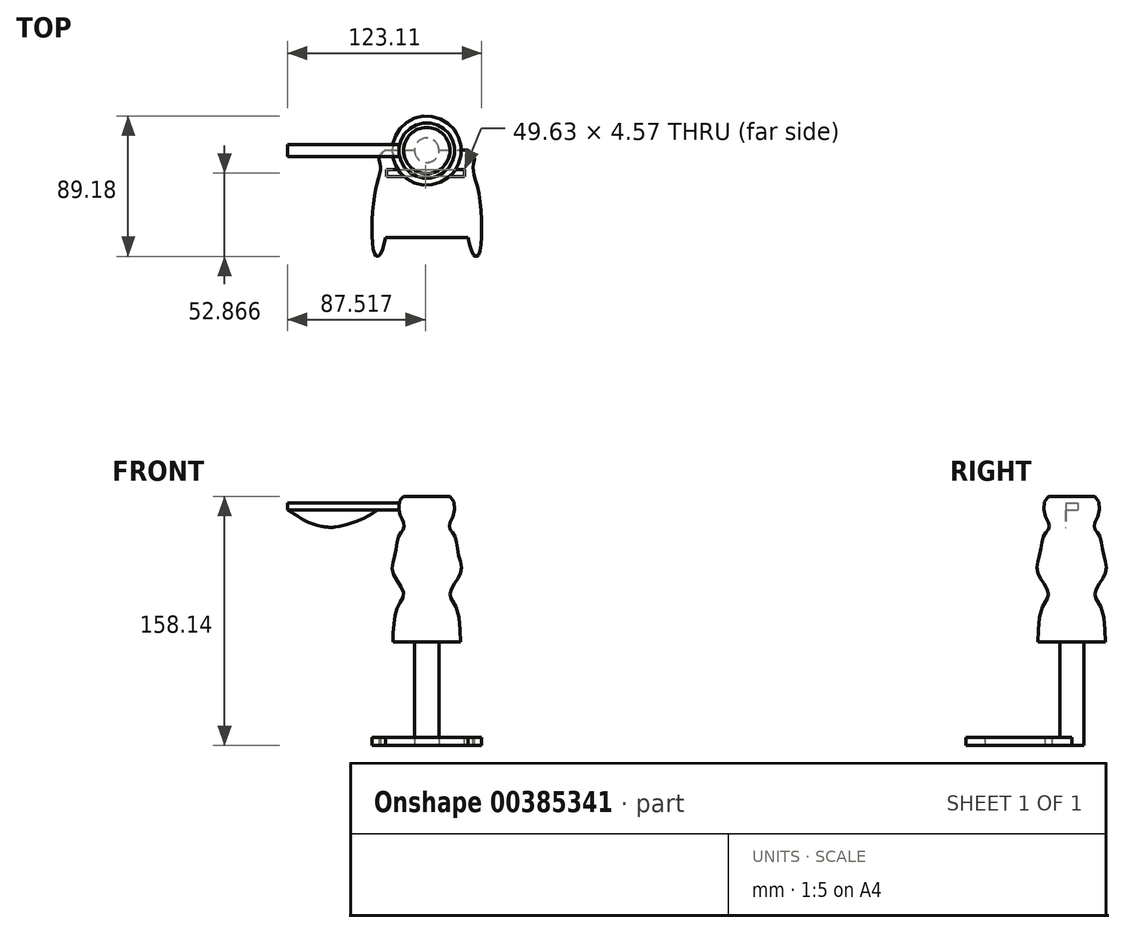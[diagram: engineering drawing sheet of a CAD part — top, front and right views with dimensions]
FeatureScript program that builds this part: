
annotation { "Feature Type Name" : "Feature", "Feature Type Description" : "" }
export const myFeature = defineFeature(function(context is Context, id is Id, definition is map)
    precondition{}
    {
        {
            var Q0;
            Q0=qCreatedBy(makeId("Top.planeOp"),FACE);
            var sketch = newSketch(context, id + "F0", { "sketchPlane" : qUnion([Q0])});
            skLineSegment(sketch, "E0", {"start": v(0, 55.4) * mm, "end": v(-26.25, 55.4) * mm});
            skFitSpline(sketch, "E1", {"points": [v(-26.25, 55.4) * mm, v(-30.26, 51.03) * mm, v(-29.53, 45.57) * mm, v(-29.9, 40.46) * mm, v(-33.17, 26.97) * mm, v(-34.63, 0) * mm, v(-32.44, -11.66) * mm, v(-30.26, -11.66) * mm, v(-26.25, 0) * mm], "startDerivative": vector(-53.73, -39.81) * mm, "endDerivative": vector(23.9, 106.11) * mm});
            skLineSegment(sketch, "E2", {"start": v(-26.25, 0) * mm, "end": v(0, 0) * mm});
            skLineSegment(sketch, "E3.MirrorCS", {"start": v(0, 55.4) * mm, "end": v(26.25, 55.4) * mm});
            skFitSpline(sketch, "E4.MirrorCS", {"points": [v(26.25, 55.4) * mm, v(30.26, 51.03) * mm, v(29.53, 45.57) * mm, v(29.9, 40.46) * mm, v(33.17, 26.97) * mm, v(34.63, 0) * mm, v(32.44, -11.66) * mm, v(30.26, -11.66) * mm, v(26.25, 0) * mm], "startDerivative": vector(53.73, -39.81) * mm, "endDerivative": vector(-23.9, 106.11) * mm});
            skLineSegment(sketch, "E5.MirrorCS", {"start": v(26.25, 0) * mm, "end": v(0, 0) * mm});
            skSolve(sketch);
        }
        {
            var Q0;
            Q0 = qSketchRegion(id + "F0", true);
            extrude(context, id + "F1", {"entities" : qUnion([Q0]), "depth" : 5.08 * mm});
        }
        {
            var Q0;
            Q0=qCreatedBy(makeId("Top.planeOp"),FACE);
            var sketch = newSketch(context, id + "F2", { "sketchPlane" : qUnion([Q0])});
            skCircle(sketch, "E6", {"center": v(0, 55.28) * mm, "radius": 7.77 * mm});
            skSolve(sketch);
        }
        {
            var Q0;
            Q0 = qSketchRegion(id + "F2", true);
            extrude(context, id + "F3", {"entities" : qUnion([Q0]), "operationType" : NewBodyOperationType.ADD, "depth" : 66.04 * mm});
        }
        {
            var Q0;
            Q0=qCreatedBy(makeId("Front.planeOp"),FACE);
            cPlane(context, id + "F4", {"entities" : qUnion([Q0]), "cplaneType" : CPlaneType.OFFSET, "offset" : 55.12 * mm, "oppositeDirection" : true, "width" : 152.4 * mm, "height" : 152.4 * mm});
        }
        {
            var Q0;
            Q0=qCreatedBy(id+"F4.planeOp",FACE);
            var sketch = newSketch(context, id + "F5", { "sketchPlane" : qUnion([Q0])});
            skLineSegment(sketch, "E7", {"start": v(0, 53.83) * mm, "end": v(0, 158.14) * mm, "construction": true});
            skLineSegment(sketch, "E8", {"start": v(0, 158.14) * mm, "end": v(-14.7, 158.14) * mm});
            skFitSpline(sketch, "E9", {"points": [v(-14.7, 158.14) * mm, v(-17.03, 155.35) * mm, v(-17.03, 146.52) * mm, v(-14.7, 141.88) * mm, v(-14.7, 137.46) * mm, v(-17.5, 133.75) * mm, v(-20.28, 120.97) * mm, v(-21.44, 109.36) * mm, v(-14.7, 96.81) * mm, v(-18.65, 87.52) * mm, v(-21.44, 65.68) * mm], "startDerivative": vector(-42.25, -32.32) * mm, "endDerivative": vector(-3.32, -157.38) * mm});
            skLineSegment(sketch, "E10", {"start": v(-21.44, 65.68) * mm, "end": v(0, 65.68) * mm});
            skLineSegment(sketch, "E11", {"start": v(0, 65.68) * mm, "end": v(0, 158.14) * mm});
            skSolve(sketch);
        }
        {
            var Q0;
            Q0 = qSketchRegion(id + "F5", true);
            var Q1;
            Q1=sQuery(id+"F5.wireOp",EDGE,"E7");
            revolve(context, id + "F6", {"operationType" : NewBodyOperationType.ADD, "entities" : qUnion([Q0]), "axis" : qUnion([Q1]), "revolveType" : RevolveType.FULL});
        }
        {
            var Q0;
            Q0=makeQuery(id+"F1.opExtrude","CAP_FACE",FACE,{"disambiguationData":[OSD([sQuery(id+"F0.wireOp",EDGE,"E0"),sQuery(id+"F0.wireOp",EDGE,"E1"),sQuery(id+"F0.wireOp",EDGE,"E2"),sQuery(id+"F0.wireOp",EDGE,"E3.MirrorCS"),sQuery(id+"F0.wireOp",EDGE,"E4.MirrorCS"),sQuery(id+"F0.wireOp",EDGE,"E5.MirrorCS")])],"isStart":false});
            var sketch = newSketch(context, id + "F7", { "sketchPlane" : qUnion([Q0])});
            skLineSegment(sketch, "E12", {"start": v(23.95, 43.02) * mm, "end": v(23.95, 38.45) * mm});
            skLineSegment(sketch, "E13", {"start": v(23.95, 38.45) * mm, "end": v(-25.68, 38.45) * mm});
            skLineSegment(sketch, "E14", {"start": v(-25.68, 38.45) * mm, "end": v(-25.5, 43.02) * mm});
            skLineSegment(sketch, "E15", {"start": v(-25.5, 43.02) * mm, "end": v(23.95, 43.02) * mm});
            skSolve(sketch);
        }
        {
            var Q0;
            Q0=makeQuery(id+"F7.imprint","IMPRINT",FACE,{"disambiguationData":[TD([[makeQuery(id+"F7.imprint","IMPRINT",EDGE,{"derivedFrom":sQuery(id+"F7.wireOp",EDGE,"E12")}),-1.0]])]});
            extrude(context, id + "F8", {"entities" : qUnion([Q0]), "operationType" : NewBodyOperationType.REMOVE, "oppositeDirection" : true, "depth" : 25.4 * mm});
        }
        {
            var Q0;
            Q0=qCreatedBy(id+"F4.planeOp",FACE);
            var sketch = newSketch(context, id + "F9", { "sketchPlane" : qUnion([Q0])});
            skLineSegment(sketch, "E16", {"start": v(-17.51, 154.17) * mm, "end": v(-17.51, 149.68) * mm});
            skLineSegment(sketch, "E17", {"start": v(-17.51, 149.68) * mm, "end": v(-88.38, 149.68) * mm});
            skLineSegment(sketch, "E18", {"start": v(-88.38, 149.68) * mm, "end": v(-88.38, 154.17) * mm});
            skLineSegment(sketch, "E19", {"start": v(-88.38, 154.17) * mm, "end": v(-17.51, 154.17) * mm});
            skSolve(sketch);
        }
        {
            var Q0;
            Q0=makeQuery(id+"F9.imprint","IMPRINT",FACE,{"disambiguationData":[TD([[makeQuery(id+"F9.imprint","IMPRINT",EDGE,{"derivedFrom":sQuery(id+"F9.wireOp",EDGE,"E16")}),-1.0]])]});
            extrude(context, id + "F10", {"entities" : qUnion([Q0]), "endBound" : BoundingType.SYMMETRIC, "depth" : 7.62 * mm});
        }
        {
            var Q0;
            Q0=makeQuery(id+"F10.opExtrude","CAP_FACE",FACE,{"disambiguationData":[OSD([sQuery(id+"F9.wireOp",EDGE,"E16"),sQuery(id+"F9.wireOp",EDGE,"E17"),sQuery(id+"F9.wireOp",EDGE,"E18"),sQuery(id+"F9.wireOp",EDGE,"E19")])],"isStart":false});
            var sketch = newSketch(context, id + "F11", { "sketchPlane" : qUnion([Q0])});
            skFitSpline(sketch, "E20", {"points": [v(-88.38, 149.68) * mm, v(-81.47, 145.31) * mm, v(-72.84, 140.9) * mm, v(-61.49, 138.58) * mm, v(-53.29, 139.63) * mm, v(-42.98, 143) * mm, v(-33.3, 148.05) * mm, v(-32.68, 149.68) * mm], "startDerivative": vector(46.07, -36.06) * mm, "endDerivative": vector(-96.65, 0) * mm});
            skSolve(sketch);
        }
        {
            var Q0;
            {var subQ0=sQuery(id+"F11.wireOp",EDGE,"E20");Q0=makeQuery(id+"F11.imprint","IMPRINT",FACE,{"disambiguationData":[TD([[makeQuery(id+"F11.imprint","IMPRINT",EDGE,{"derivedFrom":subQ0}),1.0]])]});}
            extrude(context, id + "F12", {"entities" : qUnion([Q0]), "operationType" : NewBodyOperationType.ADD, "endBound" : BoundingType.SYMMETRIC, "depth" : 0.25 * mm});
        }
    });
